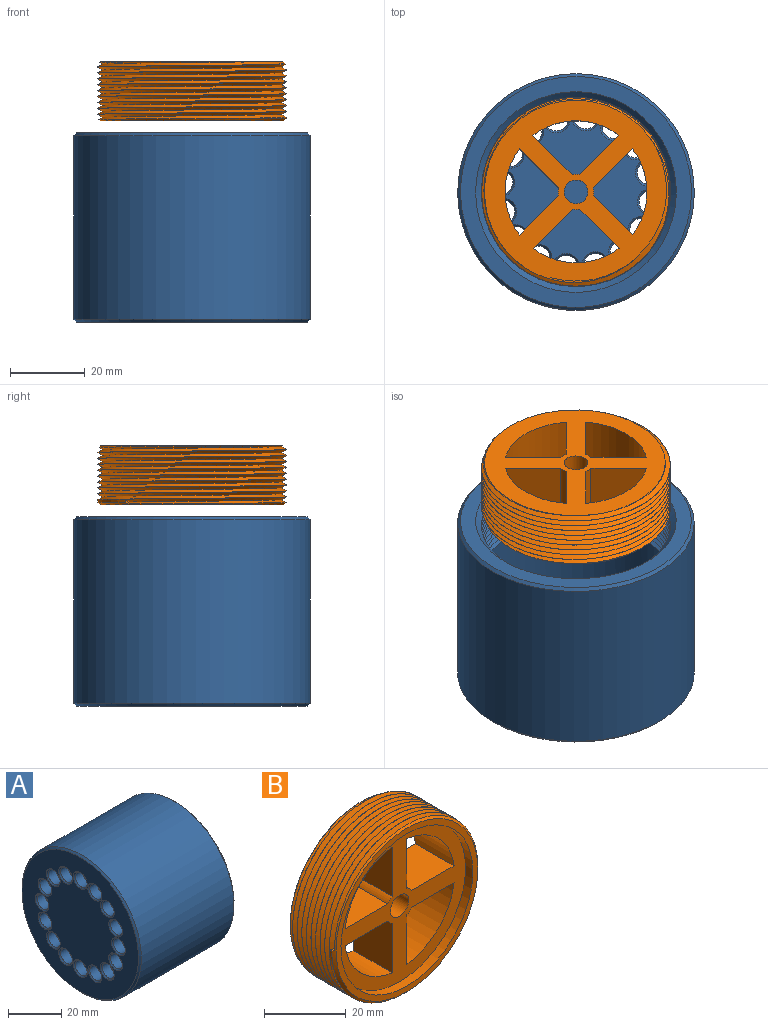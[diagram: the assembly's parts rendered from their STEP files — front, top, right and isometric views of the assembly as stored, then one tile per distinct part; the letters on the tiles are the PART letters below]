
ASSEMBLY  parts=2 mates=1
PART A: 70 faces, bbox 50.8x63.5x63.5 mm
  f0: cylinder r=25.4mm len=50.8mm, axis (1,0,0), area 4400.7mm2, adj f10,f14,f66,f68,f69
  f1: cylinder r=25.4mm len=50.8mm, axis (1,0,0), area 71.3mm2, adj f2,f31,f69
  f2: cylinder r=25.4mm len=50.8mm, axis (1,0,0), area 60mm2, adj f1,f3,f31,f67,f68,f69
  f3: cylinder r=25.4mm len=50.8mm, axis (1,0,0), area 6.1mm2, adj f2,f4,f68,f69
  f4: cylinder r=25.4mm len=50.8mm, axis (1,0,0), area 6.1mm2, adj f3,f5,f68,f69
  f5: cylinder r=25.4mm len=50.8mm, axis (1,0,0), area 6.1mm2, adj f4,f6,f68,f69
  f6: cylinder r=25.4mm len=50.8mm, axis (1,0,0), area 6.1mm2, adj f5,f7,f68,f69
  f7: cylinder r=25.4mm len=50.8mm, axis (1,0,0), area 6.1mm2, adj f6,f8,f68,f69
  f8: cylinder r=25.4mm len=50.8mm, axis (1,0,0), area 6.1mm2, adj f7,f9,f68,f69
  f9: cylinder r=25.4mm len=50.8mm, axis (1,0,0), area 6.1mm2, adj f8,f10,f68,f69
  f10: cylinder r=25.4mm len=50.8mm, axis (1,0,0), area 6.1mm2, adj f0,f9,f68,f69
  f11: plane 61.98x61.98mm, normal (1,0,0), area 739.4mm2, adj f31,f32
  f12: cylinder r=31.75mm len=63.5mm, axis (1,0,0), area 9830.1mm2, adj f32,f33
  f13: plane 61.98x61.98mm, normal (-1,0,0), area 2334.9mm2, adj f33,f49,f50,f51,f52,f53,f54,f55
  f14: plane 50.8x50.8mm, normal (1,0,0), area 1345mm2, adj f0,f34,f35,f36,f37,f38,f39,f40
  f15: cylinder r=3.17mm len=6.35mm, axis (-1,0,0), area 81.1mm2, adj f39,f63
  f16: cylinder r=3.17mm len=6.35mm, axis (-1,0,0), area 81.1mm2, adj f40,f62
  f17: cylinder r=3.17mm len=6.35mm, axis (-1,0,0), area 81.1mm2, adj f41,f61
  f18: cylinder r=3.17mm len=6.35mm, axis (-1,0,0), area 81.1mm2, adj f42,f60
  f19: cylinder r=3.17mm len=6.35mm, axis (-1,0,0), area 81.1mm2, adj f43,f59
  f20: cylinder r=3.17mm len=6.35mm, axis (-1,0,0), area 81.1mm2, adj f38,f58
  f21: cylinder r=3.17mm len=6.35mm, axis (-1,0,0), area 81.1mm2, adj f37,f57
  f22: cylinder r=3.17mm len=6.35mm, axis (-1,0,0), area 81.1mm2, adj f36,f56
  f23: cylinder r=3.17mm len=6.35mm, axis (-1,0,0), area 81.1mm2, adj f35,f55
  f24: cylinder r=3.17mm len=6.35mm, axis (-1,0,0), area 81.1mm2, adj f34,f54
  f25: cylinder r=3.17mm len=6.35mm, axis (-1,0,0), area 81.1mm2, adj f44,f53
  f26: cylinder r=3.17mm len=6.35mm, axis (-1,0,0), area 81.1mm2, adj f45,f52
  f27: cylinder r=3.17mm len=6.35mm, axis (-1,0,0), area 81.1mm2, adj f46,f51
  f28: cylinder r=3.17mm len=6.35mm, axis (-1,0,0), area 81.1mm2, adj f47,f50
  f29: cylinder r=3.17mm len=6.35mm, axis (-1,0,0), area 81.1mm2, adj f48,f49
  f30: cylinder r=3.17mm len=6.35mm, axis (-1,0,0), area 81.1mm2, adj f64,f65
  f31: cone r=25.4mm half-angle=45deg, axis (1,0,0), area 354.3mm2, adj f1,f2,f11
  f32: cone r=30.99mm half-angle=45deg, axis (-1,0,0), area 212.4mm2, adj f11,f12
  f33: cone r=31.75mm half-angle=45deg, axis (1,0,0), area 212.4mm2, adj f12,f13
  f34: cone r=3.68mm half-angle=45deg, axis (1,0,0), area 15.5mm2, adj f14,f24
  f35: cone r=3.68mm half-angle=45deg, axis (1,0,0), area 15.5mm2, adj f14,f23
  f36: cone r=3.68mm half-angle=45deg, axis (1,0,0), area 15.5mm2, adj f14,f22
  f37: cone r=3.68mm half-angle=45deg, axis (1,0,0), area 15.5mm2, adj f14,f21
  f38: cone r=3.68mm half-angle=45deg, axis (1,0,0), area 15.5mm2, adj f14,f20
  f39: cone r=3.68mm half-angle=45deg, axis (1,0,0), area 15.5mm2, adj f14,f15
  f40: cone r=3.68mm half-angle=45deg, axis (1,0,0), area 15.5mm2, adj f14,f16
  f41: cone r=3.68mm half-angle=45deg, axis (1,0,0), area 15.5mm2, adj f14,f17
  f42: cone r=3.68mm half-angle=45deg, axis (1,0,0), area 15.5mm2, adj f14,f18
  f43: cone r=3.68mm half-angle=45deg, axis (1,0,0), area 15.5mm2, adj f14,f19
  f44: cone r=3.68mm half-angle=45deg, axis (1,0,0), area 15.5mm2, adj f14,f25
  f45: cone r=3.68mm half-angle=45deg, axis (1,0,0), area 15.5mm2, adj f14,f26
  f46: cone r=3.68mm half-angle=45deg, axis (1,0,0), area 15.5mm2, adj f14,f27
  f47: cone r=3.68mm half-angle=45deg, axis (1,0,0), area 15.5mm2, adj f14,f28
  f48: cone r=3.68mm half-angle=45deg, axis (1,0,0), area 15.5mm2, adj f14,f29
  f49: cone r=3.17mm half-angle=45deg, axis (-1,0,0), area 15.5mm2, adj f13,f29
  f50: cone r=3.17mm half-angle=45deg, axis (-1,0,0), area 15.5mm2, adj f13,f28
  f51: cone r=3.17mm half-angle=45deg, axis (-1,0,0), area 15.5mm2, adj f13,f27
  f52: cone r=3.17mm half-angle=45deg, axis (-1,0,0), area 15.5mm2, adj f13,f26
  f53: cone r=3.17mm half-angle=45deg, axis (-1,0,0), area 15.5mm2, adj f13,f25
  f54: cone r=3.17mm half-angle=45deg, axis (-1,0,0), area 15.5mm2, adj f13,f24
  f55: cone r=3.17mm half-angle=45deg, axis (-1,0,0), area 15.5mm2, adj f13,f23
  f56: cone r=3.17mm half-angle=45deg, axis (-1,0,0), area 15.5mm2, adj f13,f22
  f57: cone r=3.17mm half-angle=45deg, axis (-1,0,0), area 15.5mm2, adj f13,f21
  f58: cone r=3.17mm half-angle=45deg, axis (-1,0,0), area 15.5mm2, adj f13,f20
  f59: cone r=3.17mm half-angle=45deg, axis (-1,0,0), area 15.5mm2, adj f13,f19
  f60: cone r=3.17mm half-angle=45deg, axis (-1,0,0), area 15.5mm2, adj f13,f18
  f61: cone r=3.17mm half-angle=45deg, axis (-1,0,0), area 15.5mm2, adj f13,f17
  f62: cone r=3.17mm half-angle=45deg, axis (-1,0,0), area 15.5mm2, adj f13,f16
  f63: cone r=3.17mm half-angle=45deg, axis (-1,0,0), area 15.5mm2, adj f13,f15
  f64: cone r=3.68mm half-angle=45deg, axis (1,0,0), area 15.5mm2, adj f14,f30
  f65: cone r=3.17mm half-angle=45deg, axis (-1,0,0), area 15.5mm2, adj f13,f30
  f66: plane 1.55x1.34mm, normal (0,0,-1), area 1mm2, adj f0,f68,f69
  f67: plane 1.55x1.34mm, normal (0,0,1), area 1mm2, adj f2,f68,f69
  f68: bspline ~61.76x53.48mm, area 2538.4mm2, adj f0,f2,f3,f4,f5,f6,f7,f8
  f69: bspline ~61.76x53.48mm, area 2533.3mm2, adj f0,f1,f2,f3,f4,f5,f6,f7
PART B: 27 faces, bbox 51x17.3x58.9 mm
  f0: cylinder r=19.05mm len=16.34mm, axis (0,1,0), area 331.1mm2, adj f1,f12,f20,f26
  f1: plane 14.85x13.34mm, normal (0,0,1), area 198mm2, adj f0,f2,f20,f26
  f2: cylinder r=4.76mm len=13.34mm, axis (0,1,0), area 28.3mm2, adj f1,f12,f20,f26
  f3: cylinder r=19.05mm len=16.34mm, axis (0,1,0), area 331.1mm2, adj f4,f13,f20,f26
  f4: plane 14.85x13.34mm, normal (1,0,0), area 198mm2, adj f3,f5,f20,f26
  f5: cylinder r=4.76mm len=13.34mm, axis (0,1,0), area 28.3mm2, adj f4,f13,f20,f26
  f6: cylinder r=19.05mm len=16.34mm, axis (0,1,0), area 331.1mm2, adj f7,f14,f20,f26
  f7: plane 14.85x13.34mm, normal (0,0,-1), area 198mm2, adj f6,f8,f20,f26
  f8: cylinder r=4.76mm len=13.34mm, axis (0,1,0), area 28.3mm2, adj f7,f14,f20,f26
  f9: cylinder r=19.05mm len=16.34mm, axis (0,1,0), area 331.1mm2, adj f10,f15,f20,f26
  f10: plane 14.85x13.34mm, normal (-1,0,0), area 198mm2, adj f9,f11,f20,f26
  f11: cylinder r=4.76mm len=13.34mm, axis (0,1,0), area 28.3mm2, adj f10,f15,f20,f26
  f12: plane 14.85x13.34mm, normal (1,0,0), area 198mm2, adj f0,f2,f20,f26
  f13: plane 14.85x13.34mm, normal (0,0,-1), area 198mm2, adj f3,f5,f20,f26
  f14: plane 14.85x13.34mm, normal (-1,0,0), area 198mm2, adj f6,f8,f20,f26
  f15: plane 14.85x13.34mm, normal (0,0,1), area 198mm2, adj f9,f11,f20,f26
  f16: cylinder r=3.17mm len=13.34mm, axis (0,1,0), area 266mm2, adj f20,f26
  f17: cylinder r=25.32mm len=50.64mm, axis (0,1,0), area -13.6mm2, adj f18,f21,f22,f23,f24
  f18: cone r=24.56mm half-angle=45deg, axis (0,1,0), area 143mm2, adj f17,f19,f23,f24
  f19: plane 49.12x49.12mm, normal (0,-1,0), area 252.9mm2, adj f18,f25
  f20: plane 49.52x48.94mm, normal (0,1,0), area 1067.9mm2, adj f0,f1,f2,f3,f4,f5,f6,f7
  f21: cone r=25.32mm half-angle=45deg, axis (0,-1,0), area 47.7mm2, adj f17,f20,f22,f23
  f22: bspline ~58.47x50.64mm, area 2221.1mm2, adj f17,f20,f21,f23,f24
  f23: bspline ~58.47x50.64mm, area 2329.4mm2, adj f17,f18,f20,f21,f22,f24
  f24: plane 1.36x1.3mm, normal (0,0,1), area 0.9mm2, adj f17,f18,f22,f23
  f25: cylinder r=22.86mm len=45.72mm, axis (0,-1,0), area 364.8mm2, adj f19,f26
  f26: plane 45.72x45.72mm, normal (0,-1,0), area 835.2mm2, adj f0,f1,f2,f3,f4,f5,f6,f7
PLACE A rot(axis=(-0.25,-0.94,-0.25),93.8deg) t=(55.33,-37.65,49.39)mm
PLACE B rot(axis=(0.86,-0.36,-0.36),98.4deg) t=(55.33,-37.65,68.47)mm
MATE cylindrical B.f17 <-> A.f0  axis (0,0,1) through (55.33,-37.65,60.53)mm
